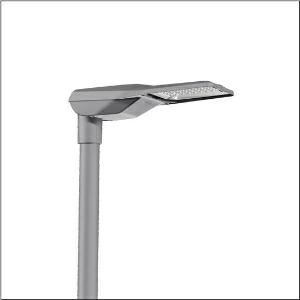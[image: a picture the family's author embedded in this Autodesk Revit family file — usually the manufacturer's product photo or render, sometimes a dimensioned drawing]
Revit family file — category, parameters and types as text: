
# Revit family: streetlight_sl_21_iq_mini___pl52_5xe2h41d08gb_a481
name_source: partatom
category: Lighting Fixtures
units: mm (PartAtom-declared; Revit-internal decimal feet)

## family parameters
Cut with Voids When Loaded = No
Host = Face
Light Source = No
Part Type = Normal
Room Calculation Point = No
Round Connector Dimension = Use Diameter
Shared = No

## types (1)
- --- (1 x LED, 5810 lm, 37.1 W, 4000K)
    Apparent Load = 37 VA
    CIE Flux Codes = 27 59 98 100 100
    Color Rendering = 70
    Color Temperature = 4000K
    Default Elevation = 1800 mm
    Description = Streetlight SL 21 iQ mini, mast luminaire, primary light control with lens, of PMMA, primary optical cover: cover, of toughened safety glass, transparent, light distribution: PL52, light emission: direct distribution, primary light characteristic: asymmetric, installation type: post-top, side-entry, LED, High Power LED, rated luminous flux: 5.810lm, luminous efficacy: 157lm/W, light colour: 740, colour temperature: 4000K, control: Auto-Match, Temp-Guard, Lumen-Switch, Night-Set, Smart-Wire, Light-Fading, Desk-Remote (wireless, voltage-free reading and setting of iQ features in the workshop via application-optimized NFC function/RFID function), optimised constant luminous flux control (CLO 2.0), presetting dimming linear, mains connection: 220..240V, AC, 50/60Hz, start of lifetime: 37W, end of service life: 39W, reduction: 18W, luminaire housing, of diecast aluminium, powder-coated, Siteco® metallic grey (DB 702S), corrosivity category C5 mid according to DIN EN ISO 12944, please order mast flange separately, inclination adjustable: 0°, 5°, 10°, 15°, sealing non-destructively replaceable, multi-level sealing system, length: 628mm, width: 235mm, height: 110mm, mast flange for spigot size: 42mm (side-entry): 5XC10008XM4, 60/48mm (side-entry/post-top): 5XC10108XM2, 76/60mm (side-entry/post-top): 5XC10108XM1, protection rating (complete): IP66, insulation class (complete): insulation class II (safety insulation), certification: CE, ENEC, ENEC+, VDE, impact resistance: IK09, permissible operating ambient temperature for outdoor applications: -40..+50°C, standard-compliant lighting for roads and squares, packaging unit: 1 piece

Light Distribution: PL52
    Height = 110 mm
    Lamp = 1 x LED
    Lamp Light Flux = 5810 lm
    Lamp Power = 37.1 W
    Lamp count = 1
    Length = 625 mm
    Luminous efficacy = 157 lm/W
    Manufacturer = Siteco
    ModVariant = No
    Model = 5XE2H41D08GB
    Number of Poles = 1
    OnlyDefault = Yes
    Power Factor = 1
    Product Name = Streetlight SL 21 iQ mini | PL52
    Product group = mast luminaire | pylon top
    ProductGroupID = 6100
    Protection Class = Protection class II
    Protection Degree = IP 66
    RLX_Detail_Level = 1
    RLX_Emergency_Light_Flux = 0 lm
    RLX_Emergency_Type = 0
    RLX_Emergency_Type_DB = No
    RlxData = <blob elided: 101813 chars, md5=ff104be9>
    Socket = socket
    Standby Power = 0 W
    System Light Flux = 5810 lm
    System Power = 37 W
    Type Comments = factory setting: luminous flux: 100 % | dim-lin: 254 | 385 mA
    Type Image = l_1003519.jpg
    URL = http://relux.com
    VarID = @adj_124273
    Voltage = 0 V
    Weight = 0.00 kg
    Width = 234 mm

## geometry (parser evidence)
native form markers: Blend x4, Sweep x11
no freeform markers — native parametric forms only
